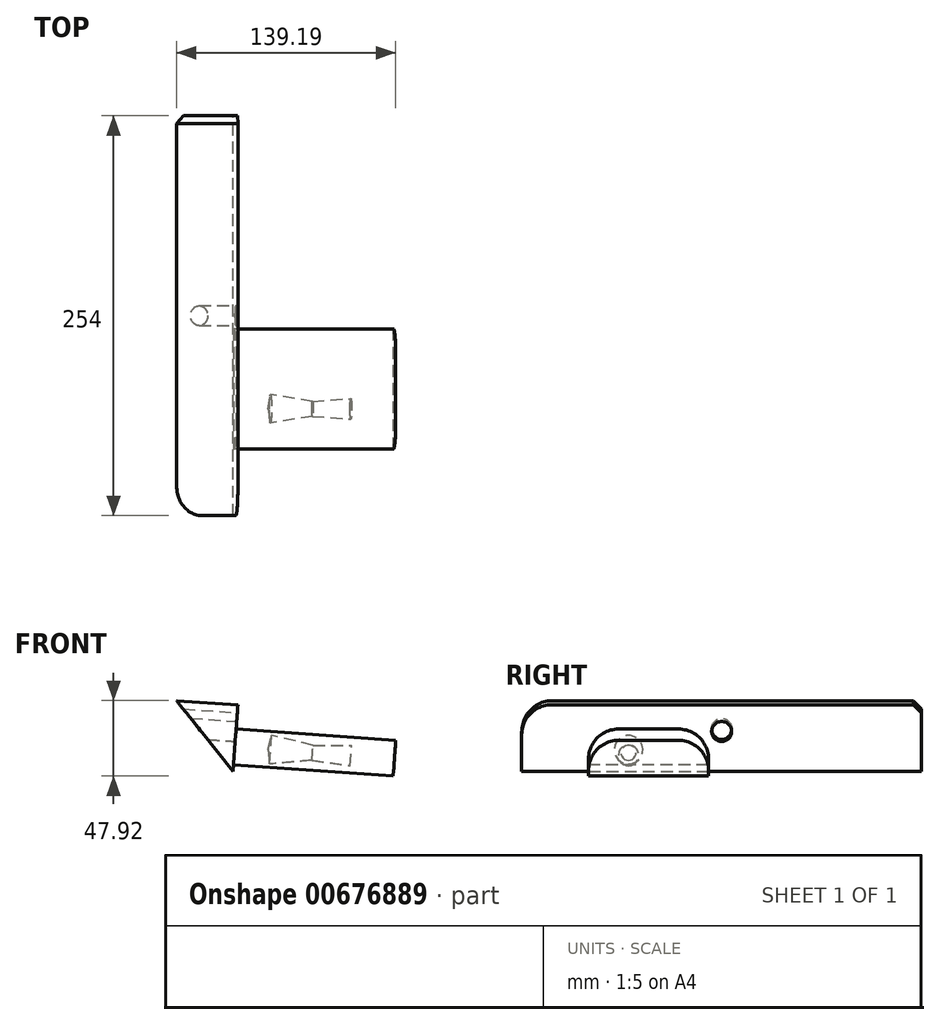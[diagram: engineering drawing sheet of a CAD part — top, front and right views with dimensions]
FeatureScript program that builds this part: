
annotation { "Feature Type Name" : "Feature", "Feature Type Description" : "" }
export const myFeature = defineFeature(function(context is Context, id is Id, definition is map)
    precondition{}
    {
        {
            var Q0;
            Q0=qCreatedBy(makeId("Front.planeOp"),FACE);
            var sketch = newSketch(context, id + "F0", { "sketchPlane" : qUnion([Q0])});
            skLineSegment(sketch, "E0", {"start": v(16.8, -16.58) * mm, "end": v(-19.15, 28.35) * mm});
            skLineSegment(sketch, "E1", {"start": v(-19.15, 28.35) * mm, "end": v(19.79, 25.78) * mm});
            skLineSegment(sketch, "E2", {"start": v(19.79, 25.78) * mm, "end": v(16.8, -16.58) * mm});
            skSolve(sketch);
        }
        {
            var Q0;
            Q0 = qSketchRegion(id + "F0", true);
            extrude(context, id + "F1", {"entities" : qUnion([Q0]), "depth" : 254 * mm, "offsetDistance" : 25.4 * mm});
        }
        {
            var Q0;
            Q0=makeQuery(id+"F1.opExtrude","SWEPT_FACE",FACE,{"disambiguationData":[OSD([sQuery(id+"F0.wireOp",EDGE,"E2")])]});
            var sketch = newSketch(context, id + "F2", { "sketchPlane" : qUnion([Q0])});
            skCircle(sketch, "E3", {"center": v(-127, 10.05) * mm, "radius": 6.35 * mm});
            skSolve(sketch);
        }
        {
            var Q0;
            Q0 = qSketchRegion(id + "F2", true);
            extrude(context, id + "F3", {"entities" : qUnion([Q0]), "operationType" : NewBodyOperationType.REMOVE, "endBound" : BoundingType.THROUGH_ALL, "oppositeDirection" : true, "depth" : 101.6 * mm, "offsetDistance" : 25.4 * mm});
        }
        {
            var Q0;
            Q0=makeQuery(id+"F1.opExtrude","SWEPT_FACE",FACE,{"disambiguationData":[OSD([sQuery(id+"F0.wireOp",EDGE,"E2")])]});
            var sketch = newSketch(context, id + "F4", { "sketchPlane" : qUnion([Q0])});
            skLineSegment(sketch, "E4.bottom", {"start": v(-135.34, -11.16) * mm, "end": v(-211.54, -11.16) * mm});
            skLineSegment(sketch, "E4.top", {"start": v(-135.34, 11.62) * mm, "end": v(-211.54, 11.62) * mm});
            skLineSegment(sketch, "E4.left", {"start": v(-135.34, -11.16) * mm, "end": v(-135.34, 11.62) * mm});
            skLineSegment(sketch, "E4.right", {"start": v(-211.54, -11.16) * mm, "end": v(-211.54, 11.62) * mm});
            skSolve(sketch);
        }
        {
            var Q0;
            Q0 = qSketchRegion(id + "F4", true);
            extrude(context, id + "F5", {"entities" : qUnion([Q0]), "operationType" : NewBodyOperationType.ADD, "depth" : 101.6 * mm, "offsetDistance" : 25.4 * mm});
        }
        {
            var Q0;
            Q0=makeQuery(id+"F5.opExtrude","SWEPT_FACE",FACE,{"disambiguationData":[OSD([sQuery(id+"F4.wireOp",EDGE,"E4.left")])]});
            cPlane(context, id + "F6", {"entities" : qUnion([Q0]), "cplaneType" : CPlaneType.OFFSET, "offset" : 50.8 * mm, "oppositeDirection" : true, "width" : 152.4 * mm, "height" : 152.4 * mm});
        }
        {
            var Q0;
            Q0=qCreatedBy(id+"F6.planeOp",FACE);
            var sketch = newSketch(context, id + "F7", { "sketchPlane" : qUnion([Q0])});
            skLineSegment(sketch, "E5", {"start": v(0, 0) * mm, "end": v(-112.8, -7.98) * mm, "construction": true});
            skLineSegment(sketch, "E6", {"start": v(-91.5, -6.47) * mm, "end": v(-91.97, 0) * mm});
            skLineSegment(sketch, "E7", {"start": v(-91.97, 0) * mm, "end": v(-67.5, 0) * mm});
            skLineSegment(sketch, "E8", {"start": v(-67.5, 0) * mm, "end": v(-41.14, 6.22) * mm});
            skLineSegment(sketch, "E9", {"start": v(-41.14, 6.22) * mm, "end": v(-39.02, -2.76) * mm});
            skLineSegment(sketch, "E10", {"start": v(-39.02, -2.76) * mm, "end": v(-91.5, -6.47) * mm});
            skSolve(sketch);
        }
        {
            var Q0;
            Q0 = qSketchRegion(id + "F7", true);
            var Q1;
            Q1=sQuery(id+"F7.wireOp",EDGE,"E5");
            revolve(context, id + "F8", {"operationType" : NewBodyOperationType.REMOVE, "entities" : qUnion([Q0]), "axis" : qUnion([Q1]), "revolveType" : RevolveType.FULL, "oppositeDirection" : true});
        }
        {
            var Q0;
            Q0=makeQuery(id+"F5.opExtrude","SWEPT_EDGE",EDGE,{"disambiguationData":[OSD([sQuery(id+"F4.wireOp",EDGE,"E4.top"),sQuery(id+"F4.wireOp",EDGE,"E4.left")])]});
            var Q1;
            Q1=makeQuery(id+"F5.opExtrude","SWEPT_EDGE",EDGE,{"disambiguationData":[OSD([sQuery(id+"F4.wireOp",EDGE,"E4.top"),sQuery(id+"F4.wireOp",EDGE,"E4.right")])]});
            var Q2;
            Q2=makeQuery(id+"F1.opExtrude","CAP_EDGE",EDGE,{"disambiguationData":[OSD([sQuery(id+"F0.wireOp",EDGE,"E1")])],"isStart":false});
            fillet(context, id + "F9", {"entities" : qUnion([Q0, Q1, Q2]), "radius" : 19.05 * mm, "tangentPropagation" : true, "allowEdgeOverflow" : false});
        }
        {
            var Q0;
            Q0=makeQuery(id+"F1.opExtrude","CAP_EDGE",EDGE,{"disambiguationData":[OSD([sQuery(id+"F0.wireOp",EDGE,"E1")])],"isStart":true});
            chamfer(context, id + "F10", {"entities" : qUnion([Q0]), "width" : 5.08 * mm, "tangentPropagation" : true});
        }
    });
